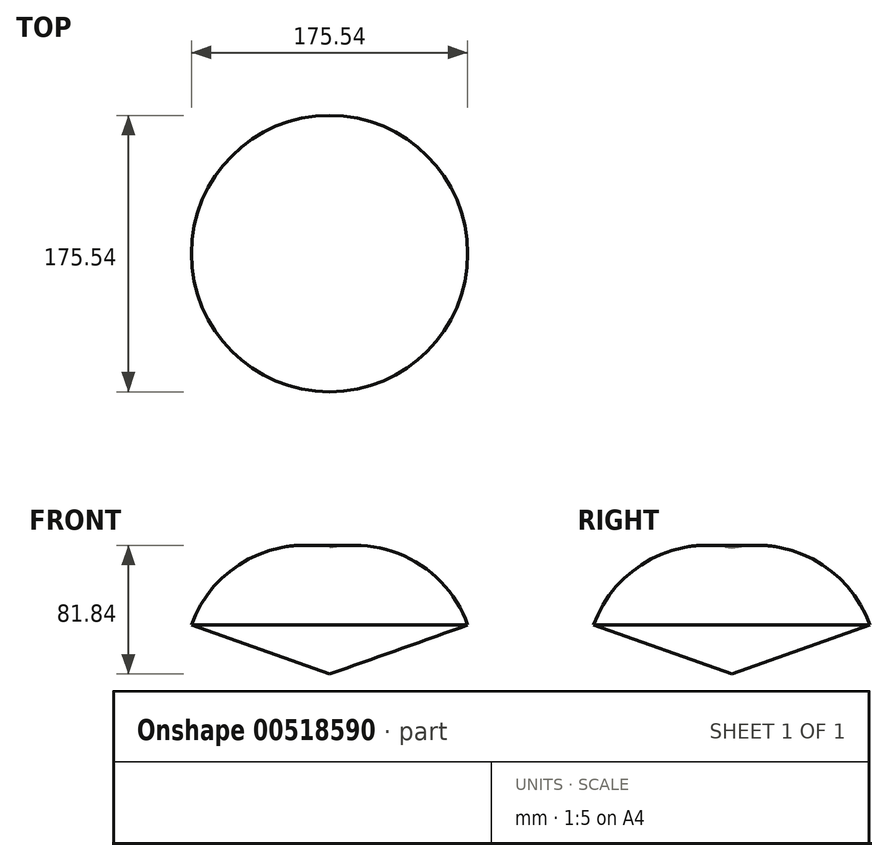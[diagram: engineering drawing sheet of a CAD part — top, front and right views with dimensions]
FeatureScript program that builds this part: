
annotation { "Feature Type Name" : "Feature", "Feature Type Description" : "" }
export const myFeature = defineFeature(function(context is Context, id is Id, definition is map)
    precondition{}
    {
        {
            var Q0;
            Q0=qCreatedBy(makeId("Front.planeOp"),FACE);
            var sketch = newSketch(context, id + "F0", { "sketchPlane" : qUnion([Q0])});
            skLineSegment(sketch, "E0", {"start": v(0, 0) * mm, "end": v(0, 69.16) * mm});
            skLineSegment(sketch, "E1", {"start": v(87.77, 100.27) * mm, "end": v(0, 69.16) * mm});
            skArc(sketch, "E2", {"start": v(0, 0) * mm, "mid": v(73.3, 24.39) * mm, "end": v(87.77, 100.27) * mm});
            skSolve(sketch);
        }
        {
            var Q0;
            Q0=sQuery(id+"F0.wireOp",EDGE,"E2");
            var Q1;
            Q1=sQuery(id+"F0.wireOp",EDGE,"E1");
            var Q2;
            Q2=sQuery(id+"F0.wireOp",EDGE,"E0");
            revolve(context, id + "F1", {"bodyType" : ToolBodyType.SURFACE, "surfaceEntities" : qUnion([Q0, Q1]), "axis" : qUnion([Q2]), "revolveType" : RevolveType.FULL});
        }
    });
